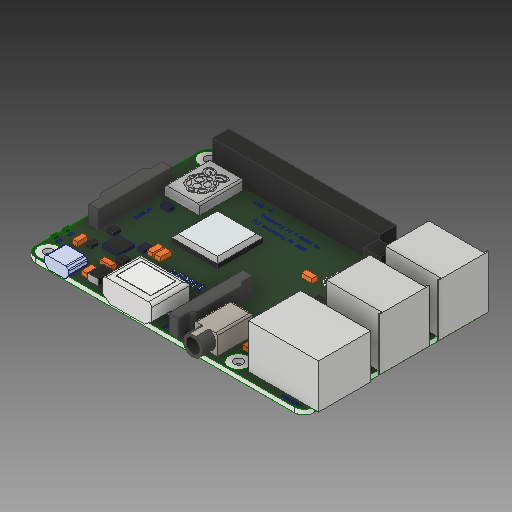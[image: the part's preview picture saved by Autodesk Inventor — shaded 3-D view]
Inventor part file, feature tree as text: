
AUTODESK INVENTOR PART (.ipt)
format: ipt  version: 2017 (Build 210142000, 142)  size: 3,965,952 bytes
history: native  units: in
note: dims shown in document units (in); Inventor stores cm internally (conversion verified against a paired STEP export)
features: other x174, fillet x3, chamfer x1, extrude x1
ambient origin geometry x8: Origin, YZ Plane, XZ Plane, XY Plane, X Axis, Y Axis, Z Axis, Center Point
bodies: Solid1 (feature_tree), Solid2 (feature_tree), Solid3 (feature_tree), Solid4 (feature_tree), Solid5 (feature_tree), Solid6 (feature_tree), Solid7 (feature_tree), Solid8 (feature_tree), Solid9 (feature_tree), Solid10 (feature_tree), Solid11 (feature_tree), Solid12 (feature_tree), Solid13 (feature_tree), Solid14 (feature_tree), Solid15 (feature_tree), Solid16 (feature_tree), Solid17 (feature_tree), Solid18 (feature_tree), Solid19 (feature_tree), Solid20 (feature_tree), Solid21 (feature_tree), Solid22 (feature_tree), Solid23 (feature_tree), Solid24 (feature_tree), Solid25 (feature_tree), Solid26 (feature_tree), Solid27 (feature_tree), Solid28 (feature_tree), Solid29 (feature_tree), Solid30 (feature_tree), Solid31 (feature_tree), Solid32 (feature_tree), Solid33 (feature_tree), Solid34 (feature_tree), Solid35 (feature_tree), Solid36 (feature_tree), Solid37 (feature_tree), Solid38 (feature_tree), Solid39 (feature_tree), Solid40 (feature_tree), Solid41 (feature_tree), Solid42 (feature_tree), Solid43 (feature_tree), Solid44 (feature_tree), Solid45 (feature_tree), Solid46 (feature_tree), Solid47 (feature_tree), Solid48 (feature_tree), Solid49 (feature_tree), Solid50 (feature_tree), Solid51 (feature_tree), Solid52 (feature_tree), Solid53 (feature_tree), Solid54 (feature_tree), Solid55 (feature_tree), Solid56 (feature_tree), Solid57 (feature_tree), Solid58 (feature_tree), Solid59 (feature_tree), Solid60 (feature_tree), Solid61 (feature_tree), Solid62 (feature_tree), Solid63 (feature_tree), Solid64 (feature_tree), Solid65 (feature_tree), Solid66 (feature_tree), Solid67 (feature_tree), Solid68 (feature_tree), Solid69 (feature_tree), Solid70 (feature_tree), Solid71 (feature_tree), Solid72 (feature_tree), Solid73 (feature_tree), Solid74 (feature_tree), Solid75 (feature_tree), Solid76 (feature_tree), Solid77 (feature_tree), Solid78 (feature_tree), Solid79 (feature_tree), Solid80 (feature_tree), Solid81 (feature_tree), Solid82 (feature_tree), Solid83 (feature_tree), Solid84 (feature_tree), Solid85 (feature_tree), Solid86 (feature_tree), Solid87 (feature_tree), Solid88 (feature_tree), Solid89 (feature_tree), Solid90 (feature_tree), Solid91 (feature_tree), Solid92 (feature_tree), Solid93 (feature_tree), Solid94 (feature_tree), Solid95 (feature_tree), Solid96 (feature_tree), Solid97 (feature_tree), Solid98 (feature_tree), Solid99 (feature_tree), Solid100 (feature_tree), Solid101 (feature_tree), Solid102 (feature_tree), Solid103 (feature_tree), Solid104 (feature_tree), Solid105 (feature_tree), Solid106 (feature_tree), Solid107 (feature_tree), Solid108 (feature_tree), Solid109 (feature_tree), Solid110 (feature_tree), Solid111 (feature_tree), Solid112 (feature_tree), Solid113 (feature_tree), Solid114 (feature_tree), Solid115 (feature_tree), Solid116 (feature_tree), Solid117 (feature_tree), Solid118 (feature_tree), Solid119 (feature_tree), Solid120 (feature_tree), Solid121 (feature_tree), Solid122 (feature_tree), Solid123 (feature_tree), Solid124 (feature_tree), Solid125 (feature_tree), Solid126 (feature_tree), Solid127 (feature_tree), Solid128 (feature_tree), Solid129 (feature_tree), Solid130 (feature_tree), Solid131 (feature_tree), Solid132 (feature_tree), Solid133 (feature_tree), Solid134 (feature_tree), Solid135 (feature_tree), Solid136 (feature_tree), Solid137 (feature_tree), Solid138 (feature_tree), Solid139 (feature_tree), Solid140 (feature_tree), Solid141 (feature_tree), Solid142 (feature_tree), Solid143 (feature_tree), Solid144 (feature_tree), Solid145 (feature_tree), Solid146 (feature_tree), Solid147 (feature_tree), Solid148 (feature_tree), Solid149 (feature_tree), Solid150 (feature_tree), Solid151 (feature_tree), Solid152 (feature_tree), Solid153 (feature_tree), Solid154 (feature_tree), Solid155 (feature_tree), Solid156 (feature_tree), Solid157 (feature_tree), Solid158 (feature_tree), Solid159 (feature_tree), Solid160 (feature_tree), Solid161 (feature_tree), Solid162 (feature_tree), Solid163 (feature_tree), Solid164 (feature_tree), Solid165 (feature_tree), Solid166 (feature_tree), Solid167 (feature_tree), Solid168 (feature_tree), Solid169 (feature_tree), Solid170 (feature_tree), Solid171 (feature_tree), Solid172 (feature_tree), Solid173 (feature_tree), Solid174 (feature_tree), Solid175 (feature_tree), Solid176 (feature_tree), Solid177 (feature_tree), Solid178 (feature_tree), Solid179 (feature_tree)
feature tree (179):
  other  "Boss-Extrude4[1]"
  other  "Boss-Extrude5[1]"
  other  "Boss-Extrude5[2]"
  other  "Boss-Extrude6"
  other  "Boss-Extrude8[1]"
  other  "Boss-Extrude8[2]"
  fillet  "Fillet2"  [1 undecoded]
  fillet  "Fillet1"  [1 undecoded]
  other  "Boss-Extrude10"
  other  "Wrap1"
  chamfer  "Chamfer1"  [1 undecoded]
  fillet  "Fillet4"  [1 undecoded]
  other  "Boss-Extrude4[2]"
  extrude  "Extrude-Thin1"  [1 undecoded]
  other  "Cut-Extrude5[1]"
  other  "Cut-Extrude5[3]"
  other  "Boss-Extrude14[1]"
  other  "Boss-Extrude14[2]"
  other  "Boss-Extrude15[1]"
  other  "Boss-Extrude16[1]"
  other  "Boss-Extrude16[2]"
  other  "Boss-Extrude16[3]"
  other  "Boss-Extrude16[4]"
  other  "Boss-Extrude16[5]"
  other  "Boss-Extrude16[6]"
  other  "Boss-Extrude16[7]"
  other  "Boss-Extrude16[8]"
  other  "Boss-Extrude16[9]"
  other  "Boss-Extrude16[10]"
  other  "Boss-Extrude16[11]"
  other  "Boss-Extrude16[12]"
  other  "Boss-Extrude15[2]"
  other  "Boss-Extrude15[3]"
  other  "Boss-Extrude15[4]"
  other  "Boss-Extrude15[5]"
  other  "Boss-Extrude15[6]"
  other  "Boss-Extrude16[13]"
  other  "Boss-Extrude16[14]"
  other  "Boss-Extrude16[15]"
  other  "Boss-Extrude17"
  other  "Boss-Extrude15[7]"
  other  "Boss-Extrude18[1]"
  other  "Boss-Extrude18[2]"
  other  "Boss-Extrude18[3]"
  other  "Boss-Extrude18[4]"
  other  "Boss-Extrude18[5]"
  other  "Boss-Extrude18[6]"
  other  "Boss-Extrude18[7]"
  other  "Boss-Extrude18[8]"
  other  "Boss-Extrude18[9]"
  other  "Boss-Extrude18[10]"
  other  "Boss-Extrude18[11]"
  other  "Boss-Extrude18[12]"
  other  "Boss-Extrude18[13]"
  other  "Boss-Extrude18[14]"
  other  "Boss-Extrude18[15]"
  other  "Boss-Extrude18[16]"
  other  "Boss-Extrude18[17]"
  other  "Boss-Extrude18[18]"
  other  "Boss-Extrude18[19]"
  other  "Boss-Extrude18[20]"
  other  "Boss-Extrude18[21]"
  other  "Boss-Extrude18[22]"
  other  "Boss-Extrude18[23]"
  other  "Boss-Extrude18[24]"
  other  "Boss-Extrude18[25]"
  other  "Boss-Extrude18[26]"
  other  "Boss-Extrude18[27]"
  other  "Boss-Extrude18[28]"
  other  "Boss-Extrude18[29]"
  other  "Boss-Extrude18[30]"
  other  "Boss-Extrude18[31]"
  other  "Boss-Extrude18[32]"
  other  "Boss-Extrude18[33]"
  other  "Boss-Extrude18[34]"
  other  "Boss-Extrude18[35]"
  other  "Boss-Extrude18[36]"
  other  "Boss-Extrude18[37]"
  other  "Boss-Extrude18[38]"
  other  "Boss-Extrude18[39]"
  other  "Boss-Extrude18[40]"
  other  "Boss-Extrude18[41]"
  other  "Boss-Extrude18[42]"
  other  "Boss-Extrude18[43]"
  other  "Boss-Extrude18[44]"
  other  "Boss-Extrude18[45]"
  other  "Boss-Extrude18[46]"
  other  "Boss-Extrude18[47]"
  other  "Boss-Extrude19"
  other  "Boss-Extrude21[1]"
  other  "Boss-Extrude21[2]"
  other  "Boss-Extrude21[3]"
  other  "Boss-Extrude21[4]"
  other  "Boss-Extrude21[5]"
  other  "Boss-Extrude21[6]"
  other  "Boss-Extrude21[7]"
  other  "Boss-Extrude21[8]"
  other  "Boss-Extrude21[9]"
  other  "Boss-Extrude21[10]"
  other  "Boss-Extrude21[11]"
  other  "Boss-Extrude21[12]"
  other  "Boss-Extrude21[13]"
  other  "Boss-Extrude21[14]"
  other  "Boss-Extrude21[15]"
  other  "Boss-Extrude21[16]"
  other  "Boss-Extrude21[17]"
  other  "Boss-Extrude21[18]"
  other  "Boss-Extrude21[19]"
  other  "Boss-Extrude21[20]"
  other  "Boss-Extrude21[21]"
  other  "Boss-Extrude21[22]"
  other  "Boss-Extrude21[23]"
  other  "Boss-Extrude21[24]"
  other  "Boss-Extrude21[25]"
  other  "Boss-Extrude21[26]"
  other  "Boss-Extrude21[27]"
  other  "Boss-Extrude21[28]"
  other  "Boss-Extrude21[29]"
  other  "Boss-Extrude21[30]"
  other  "Boss-Extrude21[31]"
  other  "Boss-Extrude21[32]"
  other  "Boss-Extrude21[33]"
  other  "Boss-Extrude21[34]"
  other  "Boss-Extrude21[35]"
  other  "Boss-Extrude21[36]"
  other  "Boss-Extrude21[37]"
  other  "Boss-Extrude21[38]"
  other  "Boss-Extrude21[39]"
  other  "Boss-Extrude21[40]"
  other  "Boss-Extrude21[41]"
  other  "Boss-Extrude21[42]"
  other  "Boss-Extrude21[43]"
  other  "Boss-Extrude21[44]"
  other  "Boss-Extrude21[45]"
  other  "Boss-Extrude21[46]"
  other  "Boss-Extrude21[47]"
  other  "Boss-Extrude21[48]"
  other  "Boss-Extrude21[49]"
  other  "Boss-Extrude21[50]"
  other  "Boss-Extrude21[51]"
  other  "Boss-Extrude21[52]"
  other  "Boss-Extrude21[53]"
  other  "Boss-Extrude21[54]"
  other  "Boss-Extrude21[55]"
  other  "Boss-Extrude21[56]"
  other  "Boss-Extrude21[57]"
  other  "Boss-Extrude21[58]"
  other  "Boss-Extrude21[59]"
  other  "Boss-Extrude21[60]"
  other  "Boss-Extrude21[61]"
  other  "Boss-Extrude21[62]"
  other  "Boss-Extrude21[63]"
  other  "Boss-Extrude21[64]"
  other  "Boss-Extrude21[65]"
  other  "Boss-Extrude21[66]"
  other  "Boss-Extrude21[67]"
  other  "Boss-Extrude21[68]"
  other  "Boss-Extrude21[69]"
  other  "Boss-Extrude21[70]"
  other  "Boss-Extrude21[71]"
  other  "Boss-Extrude21[72]"
  other  "Boss-Extrude21[73]"
  other  "Boss-Extrude21[74]"
  other  "Boss-Extrude21[75]"
  other  "Boss-Extrude21[76]"
  other  "Boss-Extrude21[77]"
  other  "Boss-Extrude21[78]"
  other  "Boss-Extrude21[79]"
  other  "Boss-Extrude21[80]"
  other  "Boss-Extrude21[81]"
  other  "Boss-Extrude21[82]"
  other  "Boss-Extrude21[83]"
  other  "Boss-Extrude21[84]"
  other  "Boss-Extrude21[85]"
  other  "Boss-Extrude21[86]"
  other  "Boss-Extrude21[87]"
  other  "Boss-Extrude21[88]"
  other  "Boss-Extrude21[89]"
  other  "Boss-Extrude22"
note: 5 required parameter values undecoded (feature->parameter linkage not recoverable at this tier; creation-order binding heuristic only, values carry confidence <= 0.55)
